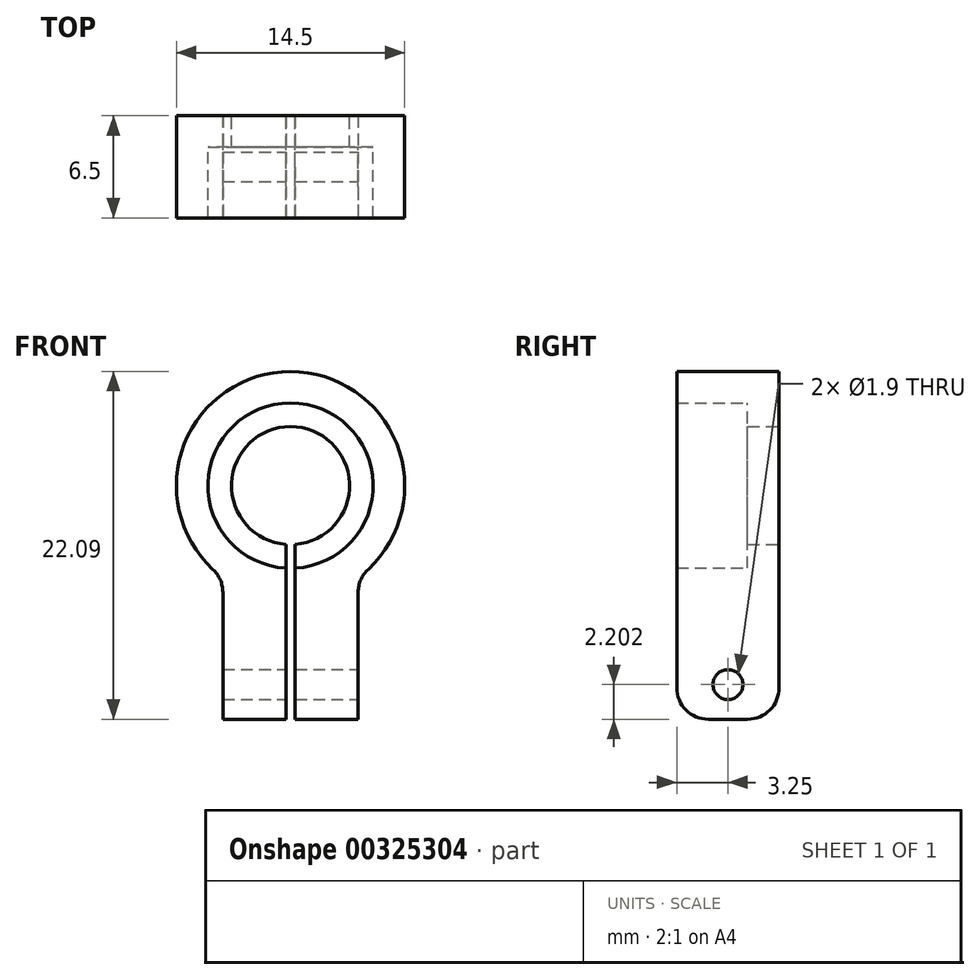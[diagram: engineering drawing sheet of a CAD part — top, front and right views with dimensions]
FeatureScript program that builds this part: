
annotation { "Feature Type Name" : "Feature", "Feature Type Description" : "" }
export const myFeature = defineFeature(function(context is Context, id is Id, definition is map)
    precondition{}
    {
        {
            var Q0;
            Q0=qCreatedBy(makeId("Front.planeOp"),FACE);
            var sketch = newSketch(context, id + "F0", { "sketchPlane" : qUnion([Q0])});
            skArc(sketch, "E0", {"start": v(4.3, -5.84) * mm, "mid": v(0, 7.25) * mm, "end": v(-4.3, -5.84) * mm});
            skLineSegment(sketch, "E1", {"start": v(-0.3, -14.84) * mm, "end": v(-4.3, -14.84) * mm});
            skLineSegment(sketch, "E2", {"start": v(-4.3, -14.84) * mm, "end": v(-4.3, -5.84) * mm});
            skLineSegment(sketch, "E3.MirrorCS", {"start": v(0.3, -14.84) * mm, "end": v(4.3, -14.84) * mm});
            skLineSegment(sketch, "E4.MirrorCS", {"start": v(4.3, -14.84) * mm, "end": v(4.3, -5.84) * mm});
            skPoint(sketch, "E5.trimOffspring.end.orphan", {"position": v(-4.3, -0.6) * mm});
            skPoint(sketch, "E6.orphan", {"position": v(4.3, -0.6) * mm});
            skArc(sketch, "E7", {"start": v(0.3, -5.24) * mm, "mid": v(0, 5.25) * mm, "end": v(-0.3, -5.24) * mm});
            skArc(sketch, "E8", {"start": v(0.3, -3.74) * mm, "mid": v(0, 3.75) * mm, "end": v(-0.3, -3.74) * mm});
            skLineSegment(sketch, "E9", {"start": v(-0.3, -14.84) * mm, "end": v(-0.3, -3.74) * mm});
            skLineSegment(sketch, "E10.MirrorCS", {"start": v(0.3, -14.84) * mm, "end": v(0.3, -3.74) * mm});
            skSolve(sketch);
        }
        {
            var Q0;
            Q0=makeQuery(id+"F0.imprint","IMPRINT",FACE,{"disambiguationData":[TD([[makeQuery(id+"F0.imprint","IMPRINT",EDGE,{"derivedFrom":sQuery(id+"F0.wireOp",EDGE,"E0")}),1.0]])]});
            extrude(context, id + "F1", {"entities" : qUnion([Q0]), "depth" : 6.5 * mm});
        }
        {
            var Q0;
            {var subQ0=sQuery(id+"F0.wireOp",EDGE,"E7");Q0=makeQuery(id+"F0.imprint","IMPRINT",FACE,{"disambiguationData":[TD([[makeQuery(id+"F0.imprint","IMPRINT",EDGE,{"derivedFrom":subQ0}),1.0]])]});}
            extrude(context, id + "F2", {"entities" : qUnion([Q0]), "operationType" : NewBodyOperationType.ADD, "depth" : 2 * mm});
        }
        {
            var Q0;
            Q0=makeQuery(id+"F1.opExtrude","SWEPT_FACE",FACE,{"disambiguationData":[OSD([sQuery(id+"F0.wireOp",EDGE,"E4.MirrorCS")])]});
            var sketch = newSketch(context, id + "F3", { "sketchPlane" : qUnion([Q0])});
            skLineSegment(sketch, "E11", {"start": v(-3.25, -5.84) * mm, "end": v(-3.25, -14.84) * mm, "construction": true});
            skCircle(sketch, "E12", {"center": v(-3.25, -12.64) * mm, "radius": 0.95 * mm});
            skSolve(sketch);
        }
        {
            var Q0;
            Q0=makeQuery(id+"F3.imprint","IMPRINT",FACE,{"disambiguationData":[TD([[makeQuery(id+"F3.imprint","IMPRINT",EDGE,{"derivedFrom":sQuery(id+"F3.wireOp",EDGE,"E12")}),1.0]])]});
            extrude(context, id + "F4", {"entities" : qUnion([Q0]), "operationType" : NewBodyOperationType.REMOVE, "oppositeDirection" : true, "depth" : 25 * mm});
        }
        {
            var Q0;
            Q0=makeQuery(id+"F1.opExtrude","CAP_EDGE",EDGE,{"disambiguationData":[OSD([sQuery(id+"F0.wireOp",EDGE,"E3.MirrorCS")])],"isStart":true});
            var Q1;
            Q1=makeQuery(id+"F1.opExtrude","CAP_EDGE",EDGE,{"disambiguationData":[OSD([sQuery(id+"F0.wireOp",EDGE,"E1")])],"isStart":true});
            var Q2;
            Q2=makeQuery(id+"F1.opExtrude","CAP_EDGE",EDGE,{"disambiguationData":[OSD([sQuery(id+"F0.wireOp",EDGE,"E3.MirrorCS")])],"isStart":false});
            var Q3;
            Q3=makeQuery(id+"F1.opExtrude","CAP_EDGE",EDGE,{"disambiguationData":[OSD([sQuery(id+"F0.wireOp",EDGE,"E1")])],"isStart":false});
            fillet(context, id + "F5", {"entities" : qUnion([Q0, Q1, Q2, Q3]), "radius" : 2 * mm, "tangentPropagation" : true, "allowEdgeOverflow" : false});
        }
        {
            var Q0;
            Q0=makeQuery(id+"F1.opExtrude","SWEPT_EDGE",EDGE,{"disambiguationData":[OSD([sQuery(id+"F0.wireOp",EDGE,"E0"),sQuery(id+"F0.wireOp",EDGE,"E4.MirrorCS")])]});
            var Q1;
            Q1=makeQuery(id+"F1.opExtrude","SWEPT_EDGE",EDGE,{"disambiguationData":[OSD([sQuery(id+"F0.wireOp",EDGE,"E0"),sQuery(id+"F0.wireOp",EDGE,"E2")])]});
            fillet(context, id + "F6", {"entities" : qUnion([Q0, Q1]), "radius" : 2 * mm, "tangentPropagation" : true, "allowEdgeOverflow" : false});
        }
    });
